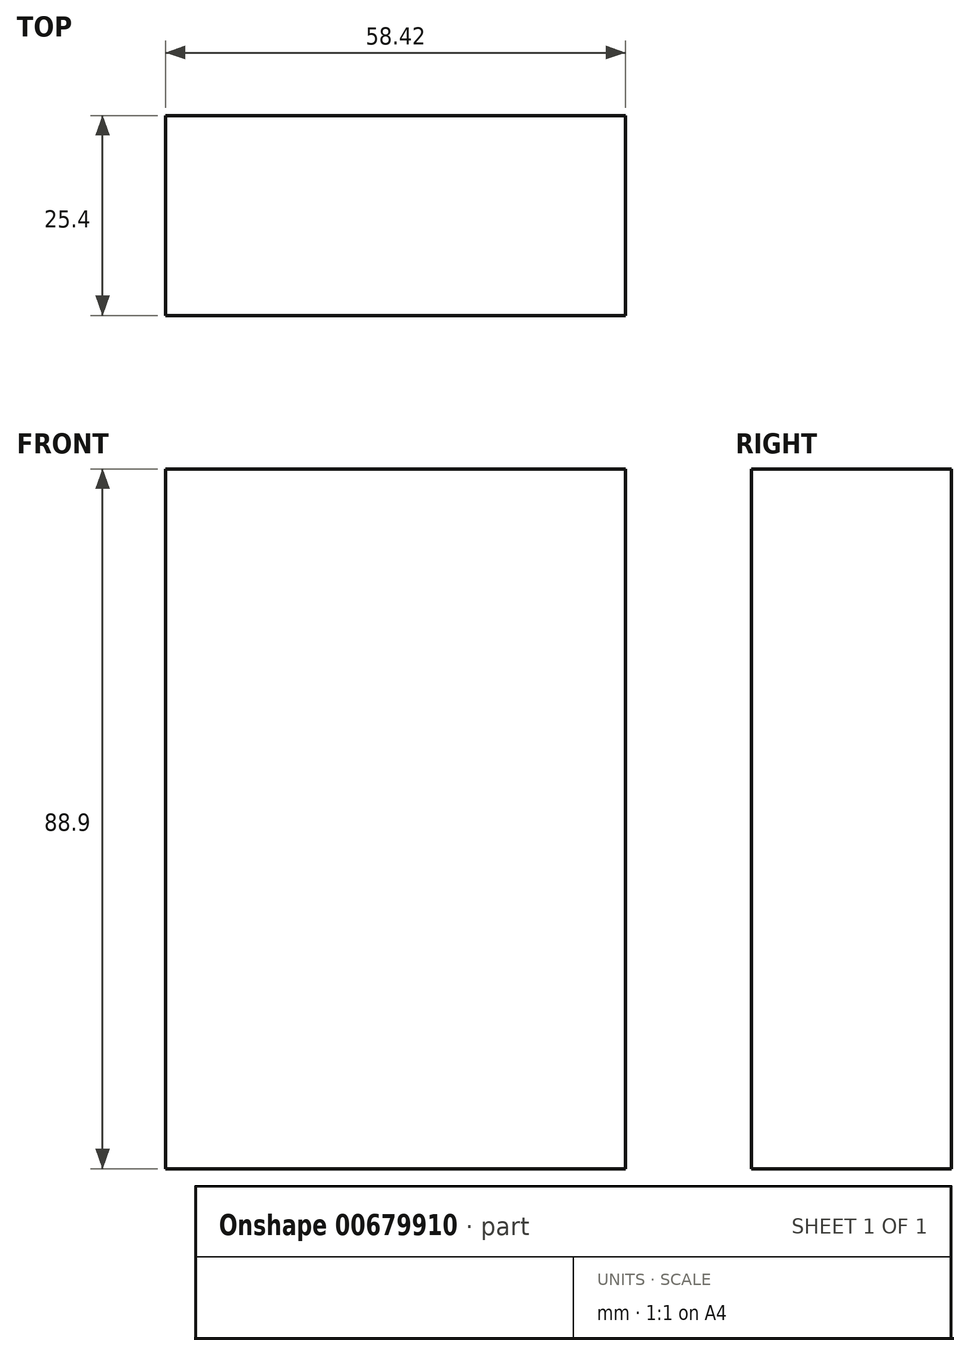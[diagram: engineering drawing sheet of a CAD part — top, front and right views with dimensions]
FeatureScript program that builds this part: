
annotation { "Feature Type Name" : "Feature", "Feature Type Description" : "" }
export const myFeature = defineFeature(function(context is Context, id is Id, definition is map)
    precondition{}
    {
        {
            var Q0;
            Q0=qCreatedBy(makeId("Front.planeOp"),FACE);
            var sketch = newSketch(context, id + "F0", { "sketchPlane" : qUnion([Q0])});
            skLineSegment(sketch, "E0.bottom", {"start": v(29.2, 44.45) * mm, "end": v(-29.21, 44.45) * mm});
            skLineSegment(sketch, "E0.top", {"start": v(29.21, -44.45) * mm, "end": v(-29.2, -44.45) * mm});
            skLineSegment(sketch, "E0.left", {"start": v(29.2, 44.45) * mm, "end": v(29.21, -44.45) * mm});
            skLineSegment(sketch, "E0.right", {"start": v(-29.21, 44.45) * mm, "end": v(-29.2, -44.45) * mm});
            skPoint(sketch, "E0.middle", {"position": v(0, 0) * mm});
            skSolve(sketch);
        }
        {
            var Q0;
            Q0 = qSketchRegion(id + "F0", true);
            extrude(context, id + "F1", {"entities" : qUnion([Q0]), "depth" : 25.4 * mm, "offsetDistance" : 25.4 * mm});
        }
    });
